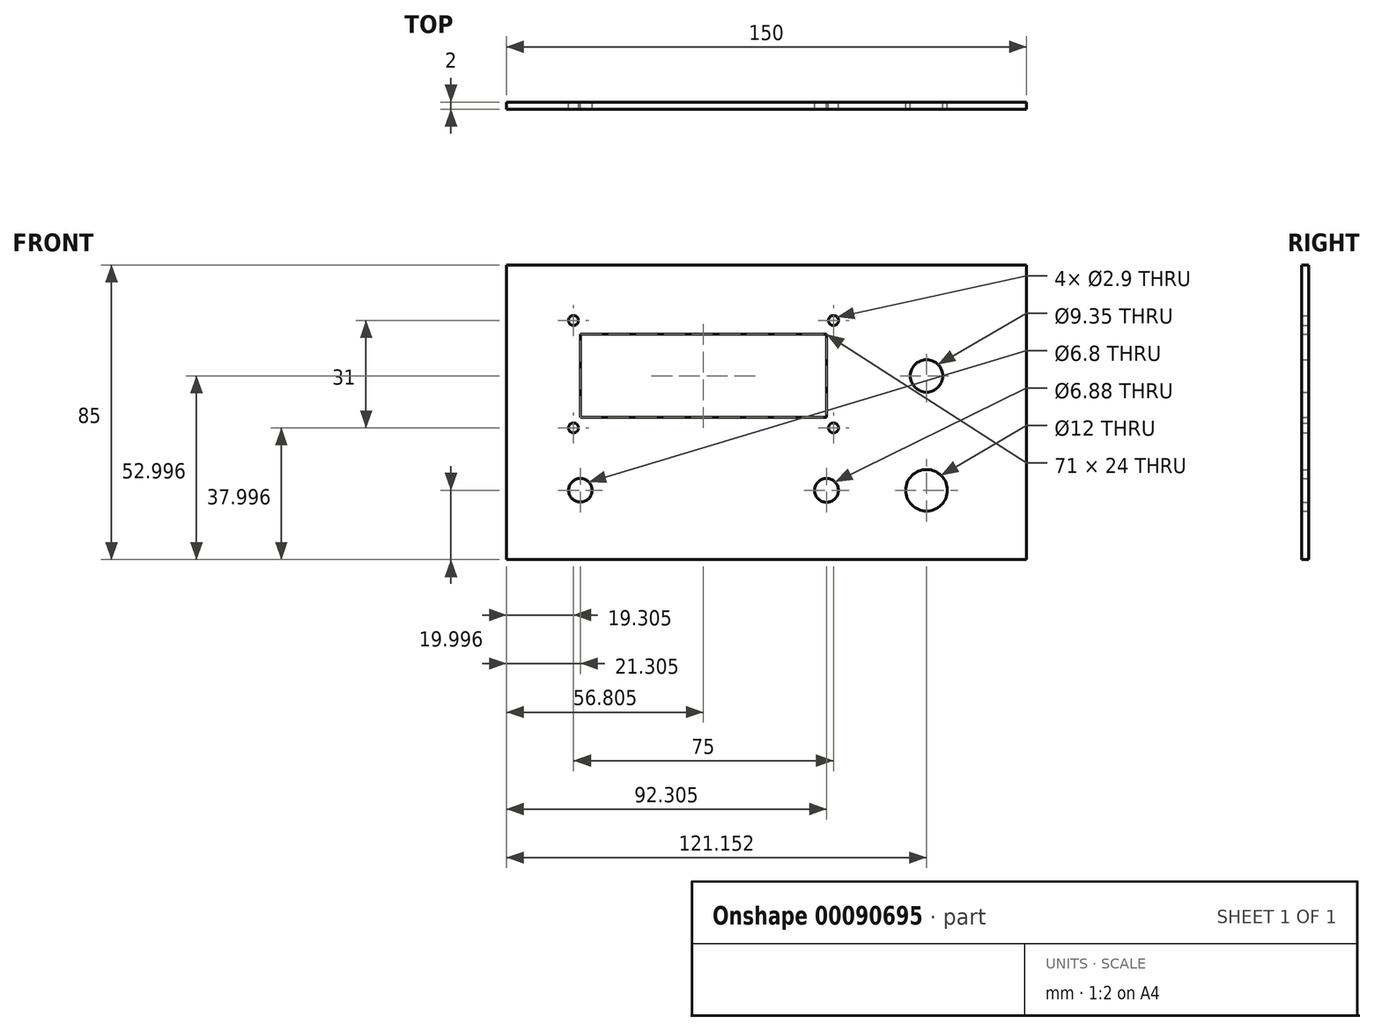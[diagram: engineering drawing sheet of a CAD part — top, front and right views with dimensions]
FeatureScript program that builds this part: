
annotation { "Feature Type Name" : "Feature", "Feature Type Description" : "" }
export const myFeature = defineFeature(function(context is Context, id is Id, definition is map)
    precondition{}
    {
        {
            var Q0;
            Q0=qCreatedBy(makeId("Front.planeOp"),FACE);
            var sketch = newSketch(context, id + "F0", { "sketchPlane" : qUnion([Q0])});
            skLineSegment(sketch, "E0.bottom", {"start": v(-227.85, -36.6) * mm, "end": v(-77.85, -36.6) * mm});
            skLineSegment(sketch, "E0.top", {"start": v(-227.85, -121.6) * mm, "end": v(-77.85, -121.6) * mm});
            skLineSegment(sketch, "E0.left", {"start": v(-227.85, -36.6) * mm, "end": v(-227.85, -121.6) * mm});
            skLineSegment(sketch, "E0.right", {"start": v(-77.85, -36.6) * mm, "end": v(-77.85, -121.6) * mm});
            skLineSegment(sketch, "E1.bottom", {"start": v(-206.54, -56.6) * mm, "end": v(-135.54, -56.6) * mm});
            skLineSegment(sketch, "E1.top", {"start": v(-206.54, -80.6) * mm, "end": v(-135.54, -80.6) * mm});
            skLineSegment(sketch, "E1.left", {"start": v(-206.54, -56.6) * mm, "end": v(-206.54, -80.6) * mm});
            skLineSegment(sketch, "E1.right", {"start": v(-135.54, -56.6) * mm, "end": v(-135.54, -80.6) * mm});
            skCircle(sketch, "E2", {"center": v(-106.7, -68.6) * mm, "radius": 4.68 * mm});
            skCircle(sketch, "E3", {"center": v(-106.7, -68.6) * mm, "radius": 7.5 * mm, "construction": true});
            skCircle(sketch, "E4", {"center": v(-206.54, -101.6) * mm, "radius": 3.4 * mm});
            skCircle(sketch, "E5", {"center": v(-206.54, -101.6) * mm, "radius": 7.36 * mm, "construction": true});
            skCircle(sketch, "E6", {"center": v(-135.54, -101.6) * mm, "radius": 3.44 * mm});
            skCircle(sketch, "E7", {"center": v(-135.54, -101.6) * mm, "radius": 7.5 * mm, "construction": true});
            skCircle(sketch, "E8", {"center": v(-106.7, -101.6) * mm, "radius": 6 * mm});
            skCircle(sketch, "E9", {"center": v(-106.7, -101.6) * mm, "radius": 7.7 * mm, "construction": true});
            skCircle(sketch, "E10", {"center": v(-106.7, -68.6) * mm, "radius": 13 * mm, "construction": true});
            skLineSegment(sketch, "E11", {"start": v(-135.54, -68.6) * mm, "end": v(-77.85, -68.6) * mm, "construction": true});
            skCircle(sketch, "E12", {"center": v(-208.54, -52.6) * mm, "radius": 1.45 * mm});
            skCircle(sketch, "E13", {"center": v(-133.54, -52.6) * mm, "radius": 1.45 * mm});
            skCircle(sketch, "E14", {"center": v(-208.54, -83.6) * mm, "radius": 1.45 * mm});
            skCircle(sketch, "E15", {"center": v(-133.54, -83.6) * mm, "radius": 1.45 * mm});
            skSolve(sketch);
        }
        {
            var Q0;
            Q0=makeQuery(id+"F0.imprint","IMPRINT",FACE,{"disambiguationData":[TD([[makeQuery(id+"F0.imprint","IMPRINT",EDGE,{"derivedFrom":sQuery(id+"F0.wireOp",EDGE,"E0.bottom")}),-1.0]])]});
            extrude(context, id + "F1", {"entities" : qUnion([Q0]), "depth" : 2 * mm});
        }
    });
